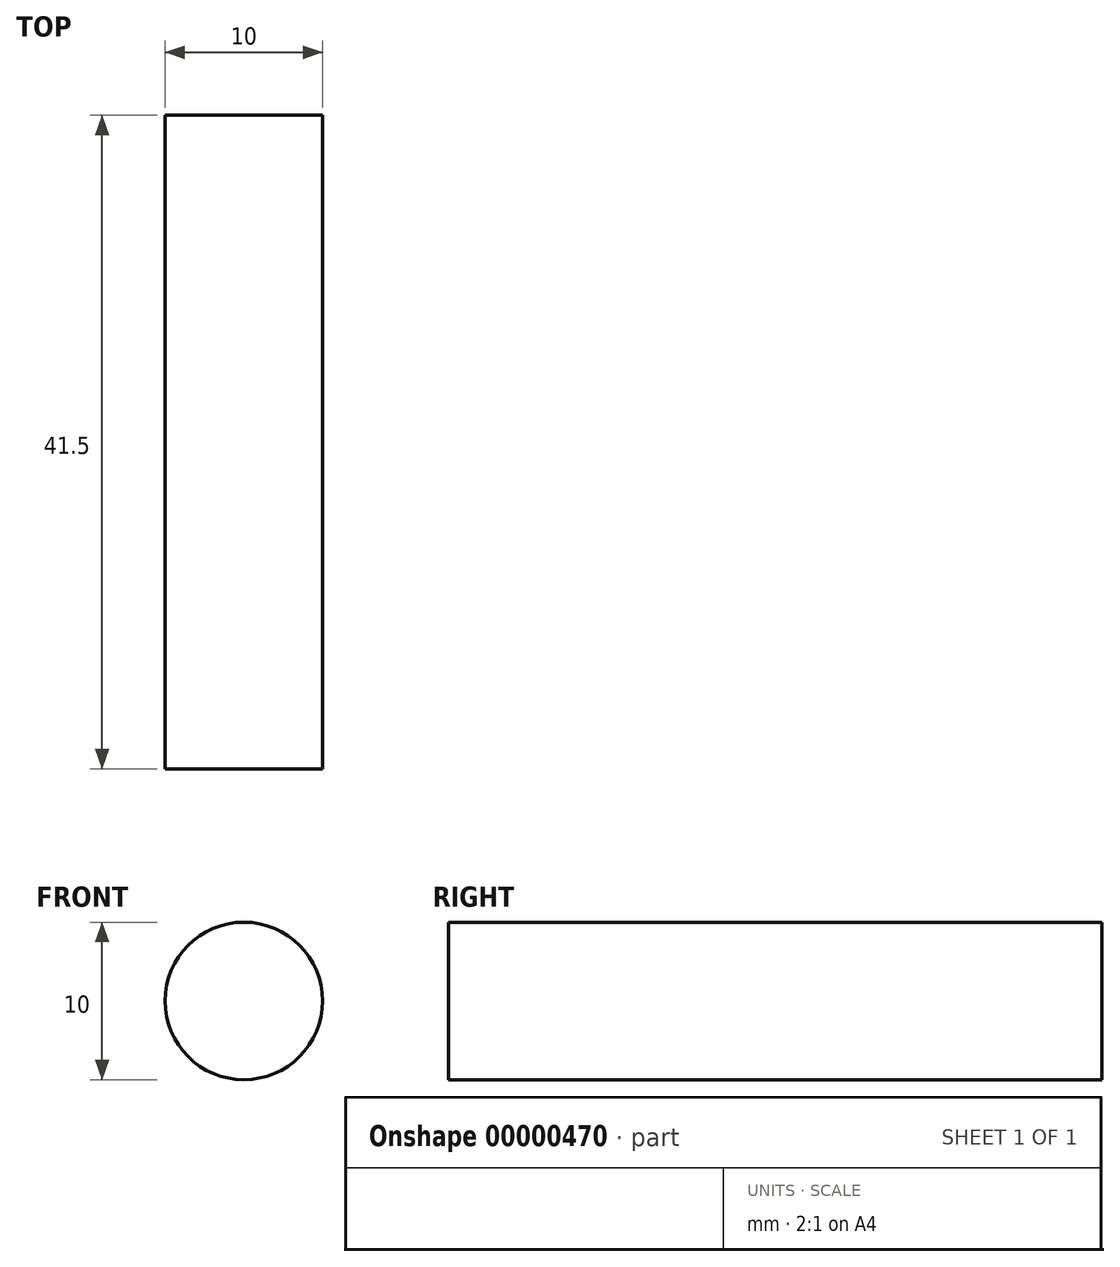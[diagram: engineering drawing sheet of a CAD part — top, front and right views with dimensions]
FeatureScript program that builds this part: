
annotation { "Feature Type Name" : "Feature", "Feature Type Description" : "" }
export const myFeature = defineFeature(function(context is Context, id is Id, definition is map)
    precondition{}
    {
        {
            var Q0;
            Q0     = qCreatedBy(makeId("Front.planeOp"), FACE);
            var sketch = newSketch(context, id + "F0", { "sketchPlane" : qUnion([Q0])});
            skCircle(sketch, "E0", {"center": v(0, 0) * mm, "radius": 5 * mm});
            skSolve(sketch);
        }
        {
            var Q0;
            Q0=makeQuery(id+"F0.imprint","IMPRINT",FACE,{"disambiguationData":[TD([[makeQuery(id+"F0.imprint","IMPRINT",EDGE,{"derivedFrom":sQuery(id+"F0.wireOp",EDGE,"E0")}),1.0]])]});
            extrude(context, id + "F1", {"entities" : qUnion([Q0]), "endBound" : BoundingType.SYMMETRIC, "oppositeDirection" : true, "depth" : 41.5 * mm});
        }
    });
